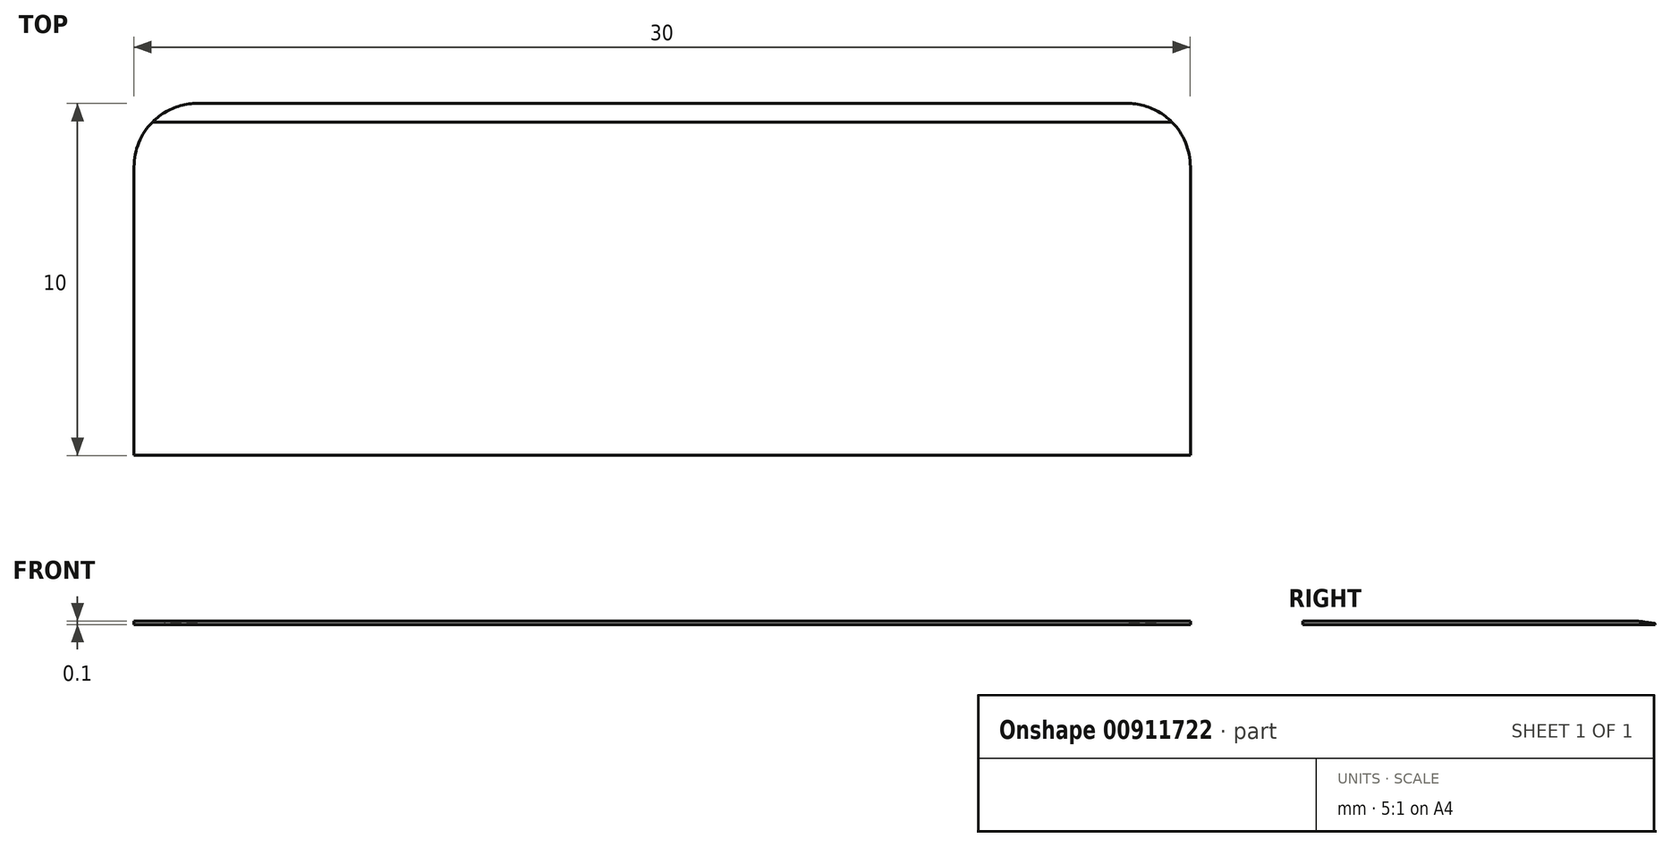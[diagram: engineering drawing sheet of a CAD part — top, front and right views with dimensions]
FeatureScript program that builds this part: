
annotation { "Feature Type Name" : "Feature", "Feature Type Description" : "" }
export const myFeature = defineFeature(function(context is Context, id is Id, definition is map)
    precondition{}
    {
        {
            var Q0;
            Q0=qCreatedBy(makeId("Top.planeOp"),FACE);
            var sketch = newSketch(context, id + "F0", { "sketchPlane" : qUnion([Q0])});
            skLineSegment(sketch, "E0.bottom", {"start": v(-11.28, 6) * mm, "end": v(18.72, 6) * mm});
            skLineSegment(sketch, "E0.top", {"start": v(-11.28, -4) * mm, "end": v(18.72, -4) * mm});
            skLineSegment(sketch, "E0.left", {"start": v(-11.28, 6) * mm, "end": v(-11.28, -4) * mm});
            skLineSegment(sketch, "E0.right", {"start": v(18.72, 6) * mm, "end": v(18.72, -4) * mm});
            skSolve(sketch);
        }
        {
            var Q0;
            Q0=makeQuery(id+"F0.imprint","IMPRINT",FACE,{"disambiguationData":[TD([[makeQuery(id+"F0.imprint","IMPRINT",EDGE,{"derivedFrom":sQuery(id+"F0.wireOp",EDGE,"E0.bottom")}),-1.0]])]});
            extrude(context, id + "F1", {"entities" : qUnion([Q0]), "depth" : 0.1 * mm, "offsetDistance" : 25 * mm});
        }
        {
            var Q0;
            Q0=makeQuery(id+"F1.opExtrude","SWEPT_FACE",FACE,{"disambiguationData":[OSD([sQuery(id+"F0.wireOp",EDGE,"E0.right")])]});
            var sketch = newSketch(context, id + "F2", { "sketchPlane" : qUnion([Q0])});
            skLineSegment(sketch, "E1", {"start": v(6, 0.03) * mm, "end": v(4.14, 0.29) * mm});
            skLineSegment(sketch, "E2", {"start": v(4.14, 0.29) * mm, "end": v(6.5, 0.44) * mm});
            skLineSegment(sketch, "E3", {"start": v(6.5, 0.44) * mm, "end": v(7.01, 0.1) * mm});
            skLineSegment(sketch, "E4", {"start": v(6, 0.03) * mm, "end": v(7.01, 0.1) * mm});
            skLineSegment(sketch, "E5", {"start": v(6, 0.03) * mm, "end": v(6, 0.03) * mm});
            skSolve(sketch);
        }
        {
            var Q0;
            Q0 = qSketchRegion(id + "F2", true);
            extrude(context, id + "F3", {"entities" : qUnion([Q0]), "operationType" : NewBodyOperationType.REMOVE, "oppositeDirection" : true, "depth" : 57.2 * mm, "offsetDistance" : 25 * mm});
        }
        {
            var Q0;
            Q0=makeQuery(id+"F1.opExtrude","SWEPT_EDGE",EDGE,{"disambiguationData":[OSD([sQuery(id+"F0.wireOp",EDGE,"E0.bottom"),sQuery(id+"F0.wireOp",EDGE,"E0.right")])]});
            var Q1;
            Q1=makeQuery(id+"F1.opExtrude","SWEPT_EDGE",EDGE,{"disambiguationData":[OSD([sQuery(id+"F0.wireOp",EDGE,"E0.bottom"),sQuery(id+"F0.wireOp",EDGE,"E0.left")])]});
            fillet(context, id + "F4", {"entities" : qUnion([Q0, Q1]), "tangentPropagation" : true, "radius" : 1.8 * mm, "defaultsChanged" : true, "vertexSettings" : [], "allowEdgeOverflow" : false});
        }
    });
